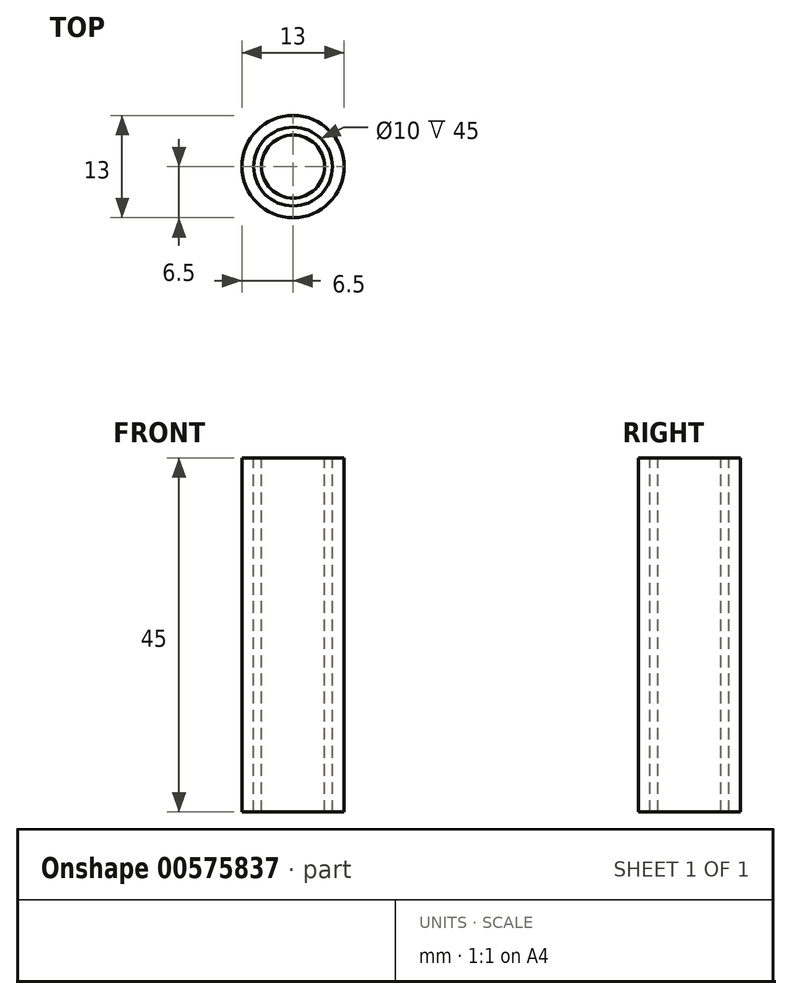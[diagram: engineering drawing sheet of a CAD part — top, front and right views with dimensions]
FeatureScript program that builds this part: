
annotation { "Feature Type Name" : "Feature", "Feature Type Description" : "" }
export const myFeature = defineFeature(function(context is Context, id is Id, definition is map)
    precondition{}
    {
        {
            var Q0;
            Q0=qCreatedBy(makeId("Top.planeOp"),FACE);
            var sketch = newSketch(context, id + "F0", { "sketchPlane" : qUnion([Q0])});
            skCircle(sketch, "E0", {"center": v(0, 0) * mm, "radius": 6.5 * mm});
            skCircle(sketch, "E1", {"center": v(0, 0) * mm, "radius": 5 * mm});
            skCircle(sketch, "E2", {"center": v(0, 0) * mm, "radius": 4 * mm});
            skSolve(sketch);
        }
        {
            var Q0;
            Q0=makeQuery(id+"F0.imprint","IMPRINT",FACE,{"disambiguationData":[TD([[makeQuery(id+"F0.imprint","IMPRINT",EDGE,{"derivedFrom":sQuery(id+"F0.wireOp",EDGE,"E2")}),1.0]])]});
            var Q1;
            Q1=makeQuery(id+"F0.imprint","IMPRINT",FACE,{"disambiguationData":[TD([[makeQuery(id+"F0.imprint","IMPRINT",EDGE,{"derivedFrom":sQuery(id+"F0.wireOp",EDGE,"E0")}),1.0]])]});
            extrude(context, id + "F1", {"entities" : qUnion([Q0, Q1]), "oppositeDirection" : true, "depth" : 45 * mm, "offsetDistance" : 25 * mm});
        }
    });
